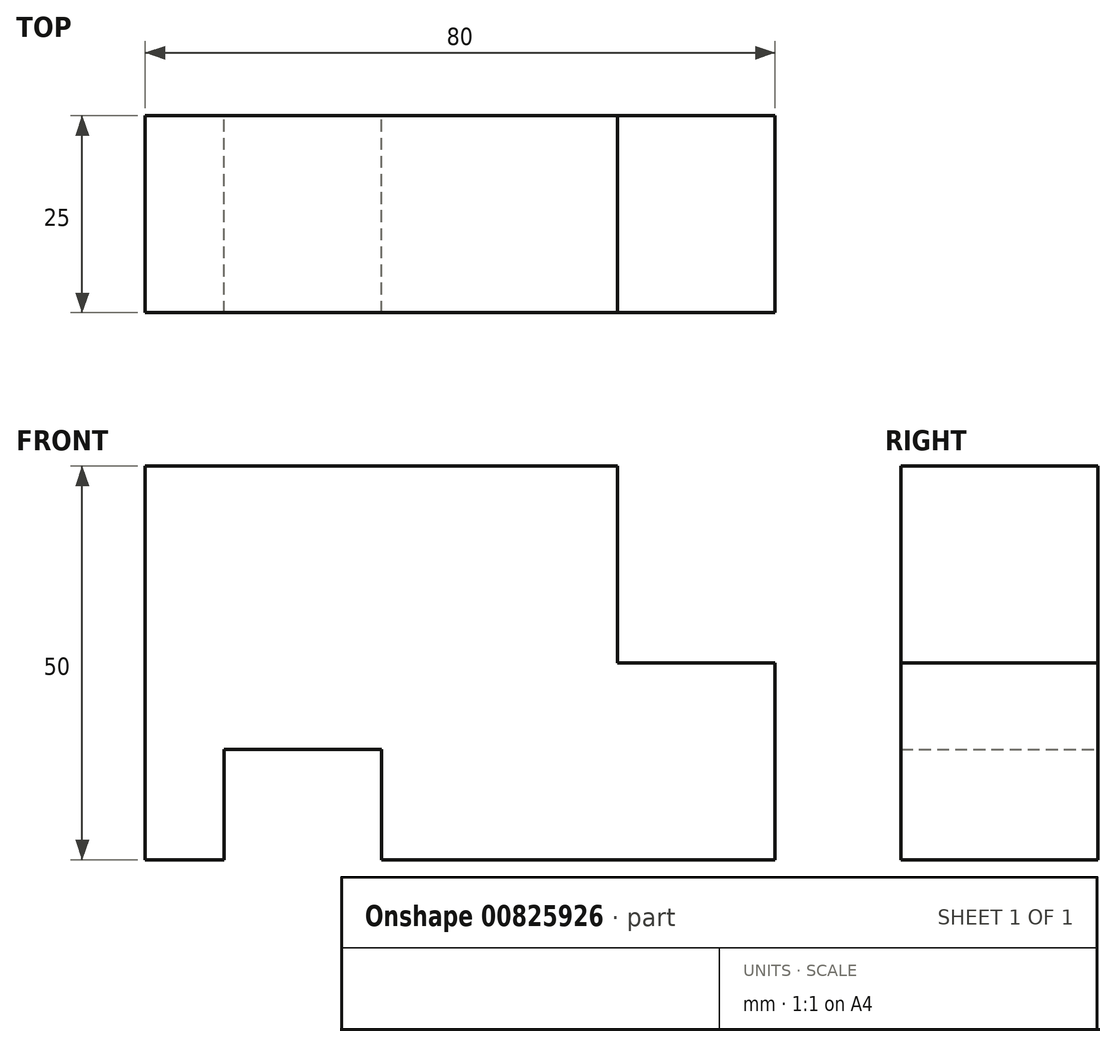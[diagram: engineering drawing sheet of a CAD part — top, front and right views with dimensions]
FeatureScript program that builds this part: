
annotation { "Feature Type Name" : "Feature", "Feature Type Description" : "" }
export const myFeature = defineFeature(function(context is Context, id is Id, definition is map)
    precondition{}
    {
        {
            var Q0;
            Q0=qCreatedBy(makeId("Front.planeOp"),FACE);
            var sketch = newSketch(context, id + "F0", { "sketchPlane" : qUnion([Q0])});
            skLineSegment(sketch, "E0", {"start": v(0, 0) * mm, "end": v(0, 50) * mm});
            skLineSegment(sketch, "E1", {"start": v(0, 50) * mm, "end": v(60, 50) * mm});
            skLineSegment(sketch, "E2", {"start": v(0, 0) * mm, "end": v(10, 0) * mm});
            skLineSegment(sketch, "E3", {"start": v(10, 0) * mm, "end": v(10, 14) * mm});
            skLineSegment(sketch, "E4", {"start": v(10, 14) * mm, "end": v(30, 14) * mm});
            skLineSegment(sketch, "E5", {"start": v(30, 14) * mm, "end": v(30, 0) * mm});
            skLineSegment(sketch, "E6", {"start": v(60, 50) * mm, "end": v(60, 25) * mm});
            skLineSegment(sketch, "E7", {"start": v(60, 25) * mm, "end": v(80, 25) * mm});
            skLineSegment(sketch, "E8", {"start": v(30, 0) * mm, "end": v(80, 0) * mm});
            skLineSegment(sketch, "E9", {"start": v(80, 25) * mm, "end": v(80, 0) * mm});
            skSolve(sketch);
        }
        {
            var Q0;
            Q0 = qSketchRegion(id + "F0", true);
            extrude(context, id + "F1", {"entities" : qUnion([Q0]), "depth" : 25 * mm, "offsetDistance" : 25 * mm});
        }
    });
